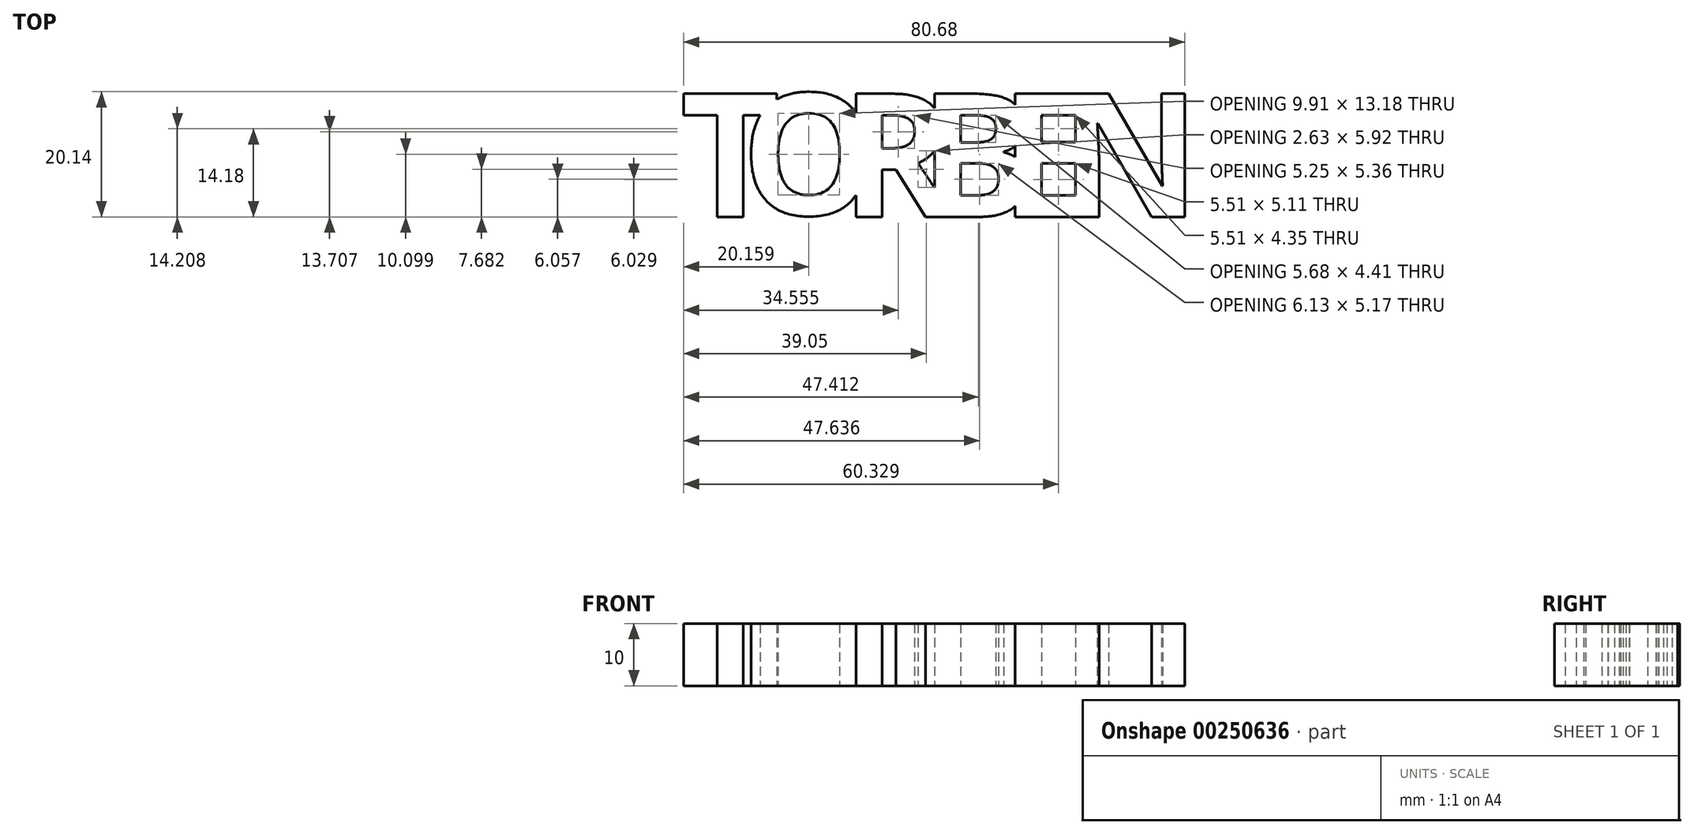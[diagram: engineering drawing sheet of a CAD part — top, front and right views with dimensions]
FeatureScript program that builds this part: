
annotation { "Feature Type Name" : "Feature", "Feature Type Description" : "" }
export const myFeature = defineFeature(function(context is Context, id is Id, definition is map)
    precondition{}
    {
        {
            var Q0;
            Q0=qCreatedBy(makeId("Top.planeOp"),FACE);
            var sketch = newSketch(context, id + "F0", { "sketchPlane" : qUnion([Q0])});
            skText(sketch, "E0", { "text": "T", "fontName": "OpenSans-Bold.ttf"});
            skText(sketch, "E1", { "text": "O", "fontName": "OpenSans-Bold.ttf"});
            skText(sketch, "E2", { "text": "R", "fontName": "OpenSans-Bold.ttf"});
            skText(sketch, "E3", { "text": "B", "fontName": "OpenSans-Bold.ttf"});
            skText(sketch, "E4", { "text": "E", "fontName": "OpenSans-Bold.ttf"});
            skText(sketch, "E5", { "text": "N", "fontName": "OpenSans-Bold.ttf"});
            const initialGuessF0  = {"E0": [-0.02007, 0.0231, 1, 0, 0.02], "E1": [-0.01024, 0.0234, 1, 0, 0.0197], "E2": [0.00572, 0.0231, 1, 0, 0.02], "E3": [0.01836, 0.0231, 1, 0, 0.02], "E4": [0.03136, 0.0231, 1, 0, 0.02], "E5": [0.04108, 0.0231, 1, 0, 0.02]};
            skSetInitialGuess(sketch, initialGuessF0);
            skSolve(sketch);
        }
        {
            var Q0;
            Q0 = qSketchRegion(id + "F0", true);
            var Q1;
            {var subQ0=sQuery(id+"F0.wireOp",EDGE,"E4.sketch_text.stroke-7");Q1=makeQuery(id+"F0.imprint","IMPRINT",FACE,{"disambiguationData":[TD([[makeQuery(id+"F0.imprint","IMPRINT",EDGE,{"derivedFrom":subQ0}),-1.0]])]});}
            extrude(context, id + "F1", {"entities" : qUnion([Q0, Q1]), "depth" : 10 * mm, "offsetDistance" : 25 * mm});
        }
    });
